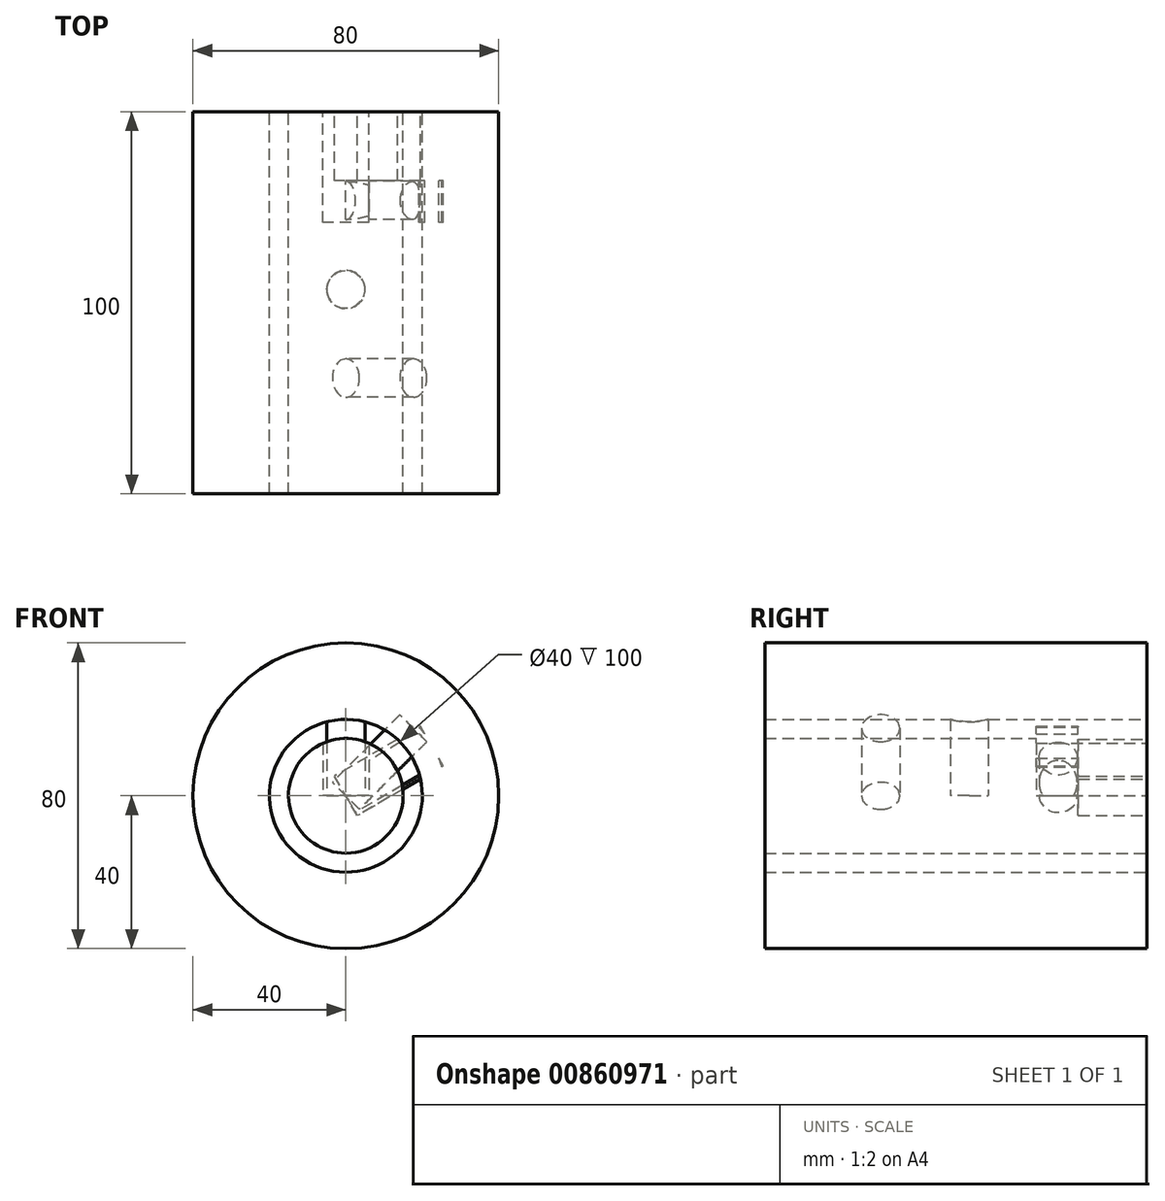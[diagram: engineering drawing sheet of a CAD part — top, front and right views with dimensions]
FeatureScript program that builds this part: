
annotation { "Feature Type Name" : "Feature", "Feature Type Description" : "" }
export const myFeature = defineFeature(function(context is Context, id is Id, definition is map)
    precondition{}
    {
        {
            var Q0;
            Q0=qCreatedBy(makeId("Front.planeOp"),FACE);
            var sketch = newSketch(context, id + "F0", { "sketchPlane" : qUnion([Q0])});
            skCircle(sketch, "E0", {"center": v(0, 0) * mm, "radius": 15 * mm});
            skSolve(sketch);
        }
        {
            var Q0;
            Q0 = qSketchRegion(id + "F0", true);
            extrude(context, id + "F1", {"entities" : qUnion([Q0]), "depth" : 100 * mm, "offsetDistance" : 25 * mm});
        }
        {
            var Q0;
            Q0=qCreatedBy(makeId("Top.planeOp"),FACE);
            var sketch = newSketch(context, id + "F2", { "sketchPlane" : qUnion([Q0])});
            skCircle(sketch, "E1", {"center": v(0, -23.23) * mm, "radius": 5 * mm});
            skLineSegment(sketch, "E2", {"start": v(0, -23.23) * mm, "end": v(0, 0) * mm, "construction": true});
            skSolve(sketch);
        }
        {
            var Q0;
            Q0 = qSketchRegion(id + "F2", true);
            extrude(context, id + "F3", {"entities" : qUnion([Q0]), "depth" : 25 * mm, "offsetDistance" : 25 * mm});
        }
        {
            var Q0;
            Q0=makeQuery(id+"F3.opExtrude","SWEPT_BODY",BODY,{"disambiguationData":[OSD([sQuery(id+"F2.wireOp",EDGE,"E1")])]});
            var Q1;
            Q1=makeQuery(id+"F1.opExtrude","SWEPT_FACE",FACE,{"disambiguationData":[OSD([sQuery(id+"F0.wireOp",EDGE,"E0")])]});
            transform(context, id + "F4", {"entities" : qUnion([Q0]), "transformType" : TransformType.ROTATION, "transformAxis" : qUnion([Q1]), "angle" : 60 * degree, "makeCopy" : false});
        }
        {
            var Q0;
            Q0=qCreatedBy(makeId("Top.planeOp"),FACE);
            var sketch = newSketch(context, id + "F5", { "sketchPlane" : qUnion([Q0])});
            skLineSegment(sketch, "E3", {"start": v(0, 0) * mm, "end": v(0, -46.5) * mm, "construction": true});
            skCircle(sketch, "E4", {"center": v(0, -46.5) * mm, "radius": 5 * mm});
            skSolve(sketch);
        }
        {
            var Q0;
            Q0=makeQuery(id+"F5.imprint","IMPRINT",FACE,{"disambiguationData":[TD([[makeQuery(id+"F5.imprint","IMPRINT",EDGE,{"derivedFrom":sQuery(id+"F5.wireOp",EDGE,"E4")}),1.0]])]});
            extrude(context, id + "F6", {"entities" : qUnion([Q0]), "depth" : 25 * mm, "offsetDistance" : 25 * mm});
        }
        {
            var Q0;
            Q0=qCreatedBy(makeId("Top.planeOp"),FACE);
            var sketch = newSketch(context, id + "F7", { "sketchPlane" : qUnion([Q0])});
            skLineSegment(sketch, "E5", {"start": v(0, 0) * mm, "end": v(0, -69.67) * mm, "construction": true});
            skCircle(sketch, "E6", {"center": v(0, -69.67) * mm, "radius": 5 * mm});
            skSolve(sketch);
        }
        {
            var Q0;
            Q0=makeQuery(id+"F7.imprint","IMPRINT",FACE,{"disambiguationData":[TD([[makeQuery(id+"F7.imprint","IMPRINT",EDGE,{"derivedFrom":sQuery(id+"F7.wireOp",EDGE,"E6")}),1.0]])]});
            extrude(context, id + "F8", {"entities" : qUnion([Q0]), "depth" : 25 * mm, "offsetDistance" : 25 * mm});
        }
        {
            var Q0;
            Q0=makeQuery(id+"F8.opExtrude","SWEPT_BODY",BODY,{"disambiguationData":[OSD([sQuery(id+"F7.wireOp",EDGE,"E6")])]});
            var Q1;
            Q1=makeQuery(id+"F1.opExtrude","SWEPT_FACE",FACE,{"disambiguationData":[OSD([sQuery(id+"F0.wireOp",EDGE,"E0")])]});
            transform(context, id + "F9", {"entities" : qUnion([Q0]), "transformType" : TransformType.ROTATION, "transformAxis" : qUnion([Q1]), "angle" : 45 * degree, "makeCopy" : false});
        }
        {
            var Q0;
            Q0=qCreatedBy(makeId("Front.planeOp"),FACE);
            var sketch = newSketch(context, id + "F10", { "sketchPlane" : qUnion([Q0])});
            skCircle(sketch, "E7", {"center": v(0, 0) * mm, "radius": 40 * mm});
            skCircle(sketch, "E8", {"center": v(0, 0) * mm, "radius": 20 * mm});
            skCircle(sketch, "E9", {"center": v(0, 0) * mm, "radius": 26.25 * mm});
            skSolve(sketch);
        }
        {
            var Q0;
            Q0=makeQuery(id+"F10.imprint","IMPRINT",FACE,{"disambiguationData":[TD([[makeQuery(id+"F10.imprint","IMPRINT",EDGE,{"derivedFrom":sQuery(id+"F10.wireOp",EDGE,"E7")}),1.0]])]});
            extrude(context, id + "F11", {"entities" : qUnion([Q0]), "depth" : 100 * mm, "offsetDistance" : 25 * mm});
        }
        {
            var Q0;
            Q0=qCreatedBy(makeId("Front.planeOp"),FACE);
            var sketch = newSketch(context, id + "F12", { "sketchPlane" : qUnion([Q0])});
            skLineSegment(sketch, "E10", {"start": v(0, 0) * mm, "end": v(-6, 0) * mm, "construction": true});
            skLineSegment(sketch, "E11", {"start": v(0, 0) * mm, "end": v(6, 0) * mm, "construction": true});
            skLineSegment(sketch, "E12", {"start": v(6, 0) * mm, "end": v(6, 26) * mm, "construction": true});
            skLineSegment(sketch, "E13.bottom", {"start": v(6, 26) * mm, "end": v(-6, 26) * mm});
            skLineSegment(sketch, "E13.top", {"start": v(6, 0) * mm, "end": v(-6, 0) * mm});
            skLineSegment(sketch, "E13.left", {"start": v(6, 26) * mm, "end": v(6, 0) * mm});
            skLineSegment(sketch, "E13.right", {"start": v(-6, 26) * mm, "end": v(-6, 0) * mm});
            skSolve(sketch);
        }
        {
            var Q0;
            Q0=makeQuery(id+"F12.imprint","IMPRINT",FACE,{"disambiguationData":[TD([[makeQuery(id+"F12.imprint","IMPRINT",EDGE,{"derivedFrom":sQuery(id+"F12.wireOp",EDGE,"E13.bottom")}),1.0]])]});
            extrude(context, id + "F13", {"entities" : qUnion([Q0]), "operationType" : NewBodyOperationType.REMOVE, "depth" : 29 * mm, "offsetDistance" : 25 * mm});
        }
        {
            var Q0;
            Q0=makeQuery(id+"F11.opExtrude","SWEPT_BODY",BODY,{"disambiguationData":[OSD([sQuery(id+"F10.wireOp",EDGE,"E7"),sQuery(id+"F10.wireOp",EDGE,"E8")])]});
            var Q1;
            Q1=makeQuery(id+"F1.opExtrude","SWEPT_FACE",FACE,{"disambiguationData":[OSD([sQuery(id+"F0.wireOp",EDGE,"E0")])]});
            transform(context, id + "F14", {"entities" : qUnion([Q0]), "transformType" : TransformType.ROTATION, "transformAxis" : qUnion([Q1]), "angle" : 60 * degree, "makeCopy" : false});
        }
        {
            var Q0;
            Q0 = qSketchRegion(id + "F12", true);
            extrude(context, id + "F15", {"entities" : qUnion([Q0]), "depth" : 18 * mm, "offsetDistance" : 25 * mm});
        }
        {
            var Q0;
            Q0=makeQuery(id+"F15.opExtrude","SWEPT_BODY",BODY,{"disambiguationData":[OSD([sQuery(id+"F12.wireOp",EDGE,"E13.bottom"),sQuery(id+"F12.wireOp",EDGE,"E13.top"),sQuery(id+"F12.wireOp",EDGE,"E13.left"),sQuery(id+"F12.wireOp",EDGE,"E13.right")])]});
            var Q1;
            Q1=makeQuery(id+"F1.opExtrude","CAP_EDGE",EDGE,{"disambiguationData":[OSD([sQuery(id+"F0.wireOp",EDGE,"E0")])],"isStart":true});
            transform(context, id + "F16", {"entities" : qUnion([Q0]), "transformType" : TransformType.ROTATION, "transformAxis" : qUnion([Q1]), "angle" : 60 * degree, "oppositeDirection" : true, "makeCopy" : false});
        }
        {
            var Q0;
            Q0=makeQuery(id+"F10.imprint","IMPRINT",FACE,{"disambiguationData":[TD([[makeQuery(id+"F10.imprint","IMPRINT",EDGE,{"derivedFrom":sQuery(id+"F10.wireOp",EDGE,"E7")}),1.0]])]});
            extrude(context, id + "F17", {"entities" : qUnion([Q0]), "operationType" : NewBodyOperationType.ADD, "depth" : 18 * mm, "offsetDistance" : 25 * mm});
        }
        {
            var Q0;
            Q0=makeQuery(id+"F10.imprint","IMPRINT",FACE,{"disambiguationData":[TD([[makeQuery(id+"F10.imprint","IMPRINT",EDGE,{"derivedFrom":sQuery(id+"F10.wireOp",EDGE,"E8")}),-1.0]])]});
            extrude(context, id + "F18", {"entities" : qUnion([Q0]), "depth" : 100 * mm, "offsetDistance" : 25 * mm});
        }
        {
            var Q0;
            Q0=makeQuery(id+"F18.opExtrude","CAP_FACE",FACE,{"disambiguationData":[OSD([sQuery(id+"F10.wireOp",EDGE,"E8"),sQuery(id+"F10.wireOp",EDGE,"E9")])],"isStart":true});
            extrude(context, id + "F19", {"entities" : qUnion([Q0]), "operationType" : NewBodyOperationType.ADD, "oppositeDirection" : true, "depth" : 60.6 * mm, "offsetDistance" : 25 * mm});
        }
    });
